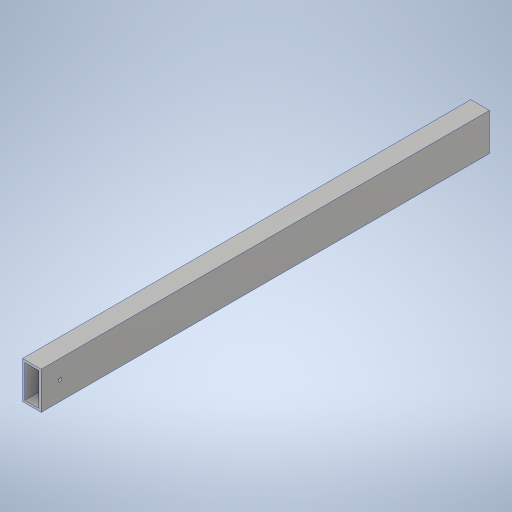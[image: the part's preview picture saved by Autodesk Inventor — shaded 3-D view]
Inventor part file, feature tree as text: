
AUTODESK INVENTOR PART (.ipt)
format: ipt  version: 2023.4 (Build 274418000, 418)  size: 256,000 bytes
history: native  units: in
note: dims shown in document units (in); Inventor stores cm internally (conversion verified against a paired STEP export)
features: extrude x1, hole x1, sketch x1
ambient origin geometry x8: Origin, YZ Plane, XZ Plane, XY Plane, X Axis, Y Axis, Z Axis, Center Point
bodies: Solid1 (feature_tree)
feature tree (3):
  extrude  "Extrusion1"  Depth=1.0in
  hole  "Hole1"  [1 undecoded]
  sketch  "Sketch2"  dims[d4=0.0in d5=1.0in d6=0.201in d7=0.75in d8=0.385in d9=0.25in d10=0.5635in d11=1.0in d12=0.8108in]
note: 1 required parameter value undecoded (feature->parameter linkage not recoverable at this tier; creation-order binding heuristic only, values carry confidence <= 0.55)
